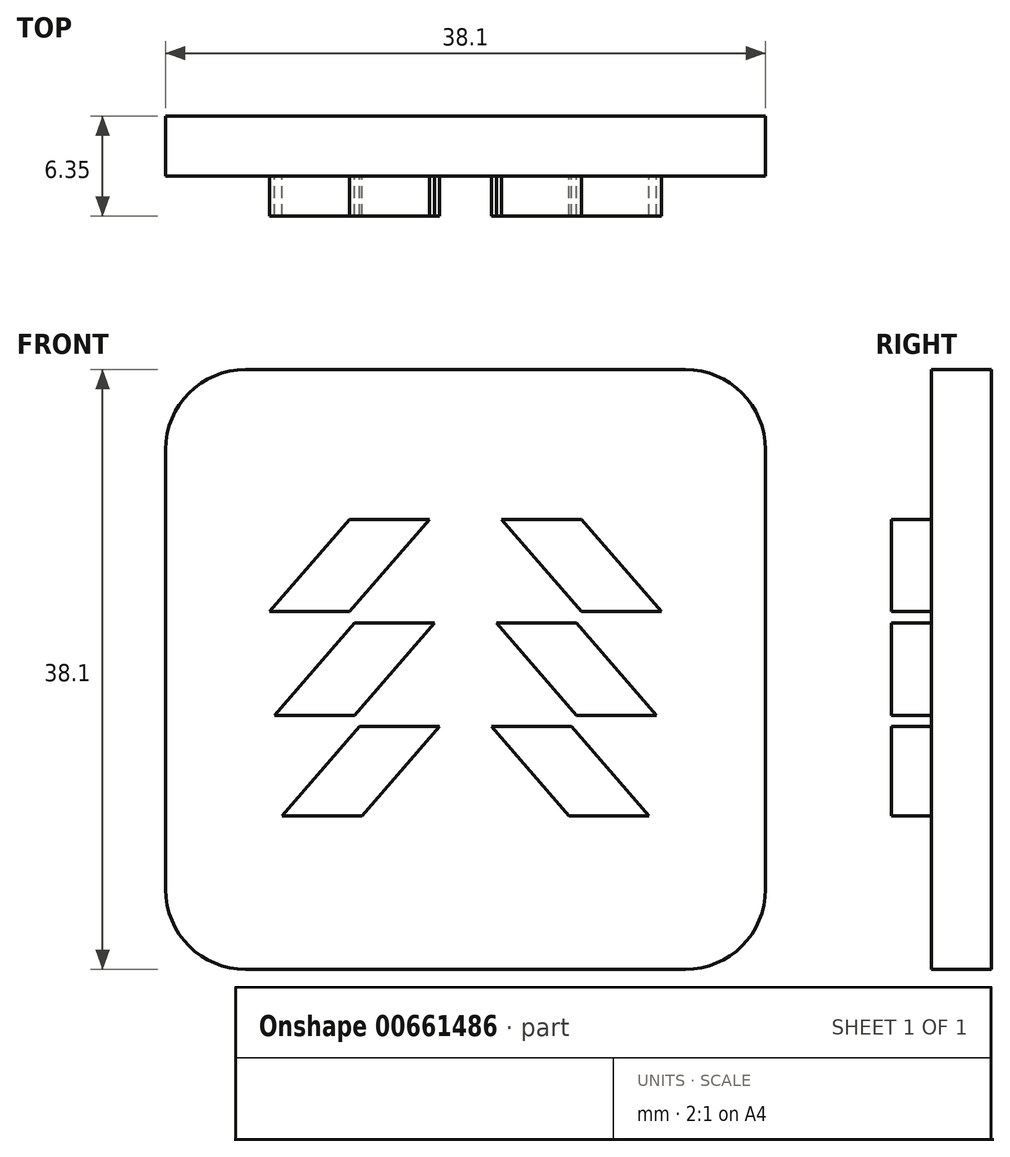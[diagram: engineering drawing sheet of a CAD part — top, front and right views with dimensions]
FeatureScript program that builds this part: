
annotation { "Feature Type Name" : "Feature", "Feature Type Description" : "" }
export const myFeature = defineFeature(function(context is Context, id is Id, definition is map)
    precondition{}
    {
        {
            var Q0;
            Q0=qCreatedBy(makeId("Front.planeOp"),FACE);
            var sketch = newSketch(context, id + "F0", { "sketchPlane" : qUnion([Q0])});
            skLineSegment(sketch, "E0.bottom", {"start": v(19.05, 19.05) * mm, "end": v(-19.05, 19.05) * mm});
            skLineSegment(sketch, "E0.top", {"start": v(19.05, -19.05) * mm, "end": v(-19.05, -19.05) * mm});
            skLineSegment(sketch, "E0.left", {"start": v(19.05, 19.05) * mm, "end": v(19.05, -19.05) * mm});
            skLineSegment(sketch, "E0.right", {"start": v(-19.05, 19.05) * mm, "end": v(-19.05, -19.05) * mm});
            skPoint(sketch, "E0.middle", {"position": v(0, 0) * mm});
            skSolve(sketch);
        }
        {
            var Q0;
            Q0=makeQuery(id+"F0.imprint","IMPRINT",FACE,{"disambiguationData":[TD([[makeQuery(id+"F0.imprint","IMPRINT",EDGE,{"derivedFrom":sQuery(id+"F0.wireOp",EDGE,"E0.bottom")}),1.0]])]});
            extrude(context, id + "F1", {"entities" : qUnion([Q0]), "depth" : 3.8 * mm, "offsetDistance" : 25.4 * mm});
        }
        {
            var Q0;
            Q0=makeQuery(id+"F1.opExtrude","SWEPT_EDGE",EDGE,{"disambiguationData":[OSD([sQuery(id+"F0.wireOp",EDGE,"E0.bottom"),sQuery(id+"F0.wireOp",EDGE,"E0.left")])]});
            var Q1;
            Q1=makeQuery(id+"F1.opExtrude","SWEPT_EDGE",EDGE,{"disambiguationData":[OSD([sQuery(id+"F0.wireOp",EDGE,"E0.bottom"),sQuery(id+"F0.wireOp",EDGE,"E0.right")])]});
            var Q2;
            Q2=makeQuery(id+"F1.opExtrude","SWEPT_EDGE",EDGE,{"disambiguationData":[OSD([sQuery(id+"F0.wireOp",EDGE,"E0.top"),sQuery(id+"F0.wireOp",EDGE,"E0.right")])]});
            var Q3;
            Q3=makeQuery(id+"F1.opExtrude","SWEPT_EDGE",EDGE,{"disambiguationData":[OSD([sQuery(id+"F0.wireOp",EDGE,"E0.top"),sQuery(id+"F0.wireOp",EDGE,"E0.left")])]});
            fillet(context, id + "F2", {"entities" : qUnion([Q0, Q1, Q2, Q3]), "radius" : 5.08 * mm, "tangentPropagation" : true, "allowEdgeOverflow" : false});
        }
        {
            var Q0;
            Q0=makeQuery(id+"F1.opExtrude","CAP_FACE",FACE,{"disambiguationData":[OSD([sQuery(id+"F0.wireOp",EDGE,"E0.bottom"),sQuery(id+"F0.wireOp",EDGE,"E0.top"),sQuery(id+"F0.wireOp",EDGE,"E0.left"),sQuery(id+"F0.wireOp",EDGE,"E0.right")])],"isStart":false});
            var sketch = newSketch(context, id + "F3", { "sketchPlane" : qUnion([Q0])});
            skLineSegment(sketch, "E1", {"start": v(0, 0) * mm, "end": v(0, 19.05) * mm});
            skLineSegment(sketch, "E2", {"start": v(0, 0) * mm, "end": v(0, -19.05) * mm});
            skLineSegment(sketch, "E3", {"start": v(0, -19.05) * mm, "end": v(0, 9.53) * mm});
            skLineSegment(sketch, "E4", {"start": v(-2.29, 9.53) * mm, "end": v(-7.37, 9.53) * mm});
            skLineSegment(sketch, "E5", {"start": v(-7.37, 3.68) * mm, "end": v(-12.45, 3.68) * mm});
            skLineSegment(sketch, "E6", {"start": v(-7.37, 9.53) * mm, "end": v(-12.45, 3.68) * mm});
            skLineSegment(sketch, "E7", {"start": v(-7.37, 3.68) * mm, "end": v(-2.29, 9.53) * mm});
            skLineSegment(sketch, "E8", {"start": v(-7.05, 2.94) * mm, "end": v(-1.97, 2.94) * mm});
            skLineSegment(sketch, "E9", {"start": v(-7.05, 2.94) * mm, "end": v(-12.13, -2.9) * mm});
            skLineSegment(sketch, "E10", {"start": v(-12.13, -2.9) * mm, "end": v(-7.05, -2.9) * mm});
            skLineSegment(sketch, "E11", {"start": v(-7.05, -2.9) * mm, "end": v(-1.97, 2.94) * mm});
            skLineSegment(sketch, "E12", {"start": v(-6.74, -3.63) * mm, "end": v(-1.66, -3.63) * mm});
            skLineSegment(sketch, "E13", {"start": v(-6.74, -3.63) * mm, "end": v(-11.66, -9.3) * mm});
            skLineSegment(sketch, "E14", {"start": v(-11.66, -9.3) * mm, "end": v(-6.58, -9.3) * mm});
            skLineSegment(sketch, "E15", {"start": v(-6.58, -9.3) * mm, "end": v(-1.66, -3.63) * mm});
            skLineSegment(sketch, "E16", {"start": v(0, 19.05) * mm, "end": v(0, -19.05) * mm});
            skLineSegment(sketch, "E17.MirrorCS", {"start": v(7.37, 3.68) * mm, "end": v(2.29, 9.53) * mm});
            skLineSegment(sketch, "E18.MirrorCS", {"start": v(2.29, 9.53) * mm, "end": v(7.37, 9.53) * mm});
            skLineSegment(sketch, "E19.MirrorCS", {"start": v(7.37, 9.53) * mm, "end": v(12.45, 3.68) * mm});
            skLineSegment(sketch, "E20.MirrorCS", {"start": v(7.37, 3.68) * mm, "end": v(12.45, 3.68) * mm});
            skLineSegment(sketch, "E21.MirrorCS", {"start": v(7.05, 2.94) * mm, "end": v(1.97, 2.94) * mm});
            skLineSegment(sketch, "E22.MirrorCS", {"start": v(7.05, 2.94) * mm, "end": v(12.13, -2.9) * mm});
            skLineSegment(sketch, "E23.MirrorCS", {"start": v(12.13, -2.9) * mm, "end": v(7.05, -2.9) * mm});
            skLineSegment(sketch, "E24.MirrorCS", {"start": v(7.05, -2.9) * mm, "end": v(1.97, 2.94) * mm});
            skLineSegment(sketch, "E25.MirrorCS", {"start": v(6.74, -3.63) * mm, "end": v(1.66, -3.63) * mm});
            skLineSegment(sketch, "E26.MirrorCS", {"start": v(6.74, -3.63) * mm, "end": v(11.66, -9.3) * mm});
            skLineSegment(sketch, "E27.MirrorCS", {"start": v(11.66, -9.3) * mm, "end": v(6.58, -9.3) * mm});
            skLineSegment(sketch, "E28.MirrorCS", {"start": v(6.58, -9.3) * mm, "end": v(1.66, -3.63) * mm});
            skSolve(sketch);
        }
        {
            var Q0;
            Q0=makeQuery(id+"F3.imprint","IMPRINT",FACE,{"disambiguationData":[TD([[makeQuery(id+"F3.imprint","IMPRINT",EDGE,{"derivedFrom":sQuery(id+"F3.wireOp",EDGE,"E4")}),1.0]])]});
            var Q1;
            Q1=makeQuery(id+"F3.imprint","IMPRINT",FACE,{"disambiguationData":[TD([[makeQuery(id+"F3.imprint","IMPRINT",EDGE,{"derivedFrom":sQuery(id+"F3.wireOp",EDGE,"E8")}),-1.0]])]});
            var Q2;
            Q2=makeQuery(id+"F3.imprint","IMPRINT",FACE,{"disambiguationData":[TD([[makeQuery(id+"F3.imprint","IMPRINT",EDGE,{"derivedFrom":sQuery(id+"F3.wireOp",EDGE,"E12")}),-1.0]])]});
            var Q3;
            Q3=makeQuery(id+"F3.imprint","IMPRINT",FACE,{"disambiguationData":[TD([[makeQuery(id+"F3.imprint","IMPRINT",EDGE,{"derivedFrom":sQuery(id+"F3.wireOp",EDGE,"E25.MirrorCS")}),1.0]])]});
            var Q4;
            Q4=makeQuery(id+"F3.imprint","IMPRINT",FACE,{"disambiguationData":[TD([[makeQuery(id+"F3.imprint","IMPRINT",EDGE,{"derivedFrom":sQuery(id+"F3.wireOp",EDGE,"E21.MirrorCS")}),1.0]])]});
            var Q5;
            Q5=makeQuery(id+"F3.imprint","IMPRINT",FACE,{"disambiguationData":[TD([[makeQuery(id+"F3.imprint","IMPRINT",EDGE,{"derivedFrom":sQuery(id+"F3.wireOp",EDGE,"E17.MirrorCS")}),-1.0]])]});
            extrude(context, id + "F4", {"entities" : qUnion([Q0, Q1, Q2, Q3, Q4, Q5]), "operationType" : NewBodyOperationType.ADD, "depth" : 2.54 * mm, "offsetDistance" : 25.4 * mm});
        }
    });
